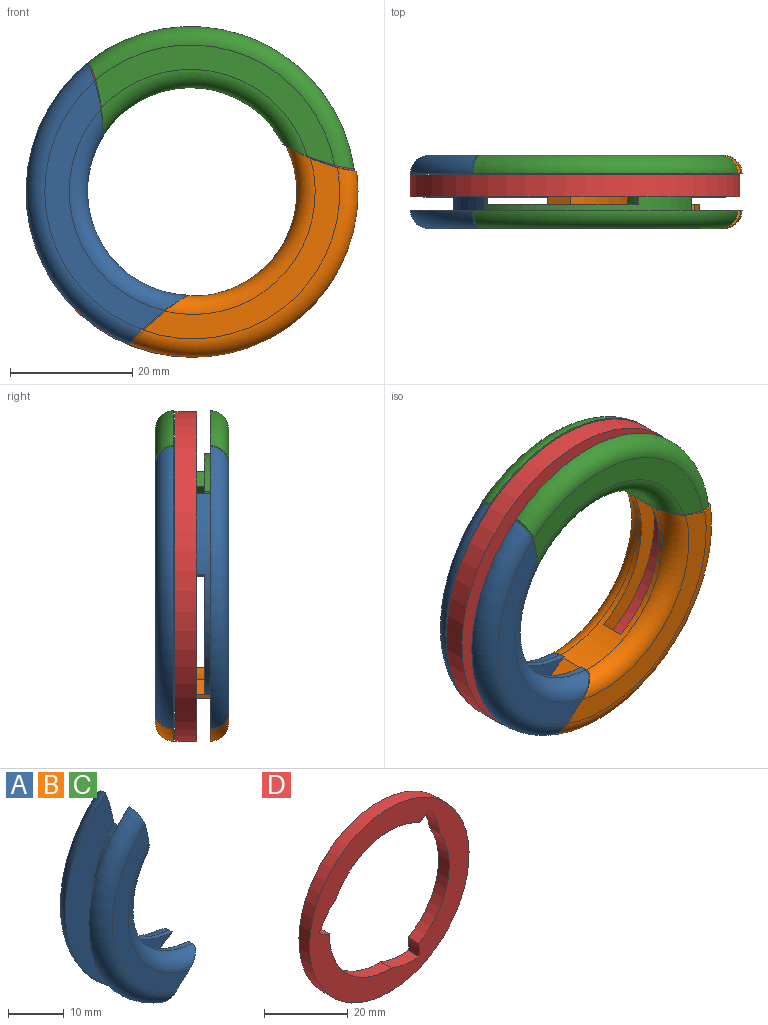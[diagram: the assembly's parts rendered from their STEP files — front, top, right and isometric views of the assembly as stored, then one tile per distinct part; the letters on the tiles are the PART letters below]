
ASSEMBLY  parts=4 mates=6
PART A: 16 faces, bbox 28.5x12x50.5 mm
  f0: cylinder r=20mm len=33.09mm, axis (0,1,0), area 142.1mm2, adj f1,f3,f4,f5,f7,f8,f9,f11
  f1: cylinder r=10mm len=4mm, axis (0,1,0), area 12.1mm2, adj f0,f2,f7,f11
  f2: cylinder r=17mm len=26.09mm, axis (0,1,0), area 109.6mm2, adj f1,f3,f5,f7,f9,f11,f12,f15
  f3: cylinder r=32mm len=12.09mm, axis (0,1,0), area 90.9mm2, adj f0,f2,f4,f6,f8,f10,f12,f13
  f4: plane 46.28x22.57mm, normal (0,-1,0), area 344.5mm2, adj f0,f3,f5,f14
  f5: cylinder r=32mm len=9.29mm, axis (0,-1,0), area 36.5mm2, adj f0,f2,f4,f6,f7,f14,f15
  f6: plane 40.84x19.57mm, normal (0,1,0), area 184.3mm2, adj f3,f5,f14,f15
  f7: plane 19.87x19.3mm, normal (0,-1,0), area 79.3mm2, adj f0,f1,f2,f5
  f8: plane 46.28x22.57mm, normal (0,1,0), area 344.5mm2, adj f0,f3,f9,f13
  f9: cylinder r=32mm len=9.29mm, axis (0,1,0), area 36.5mm2, adj f0,f2,f8,f10,f11,f12,f13
  f10: plane 40.84x19.57mm, normal (0,-1,0), area 184.3mm2, adj f3,f9,f12,f13
  f11: plane 19.87x19.3mm, normal (0,1,0), area 79.3mm2, adj f0,f1,f2,f9
  f12: torus R=20mm, axis (0,1,0), area 178.5mm2, adj f2,f3,f9,f10
  f13: torus R=24mm, axis (0,1,0), area 255.7mm2, adj f3,f8,f9,f10
  f14: torus R=24mm, axis (0,-1,0), area 255.7mm2, adj f3,f4,f5,f6
  f15: torus R=20mm, axis (0,-1,0), area 178.5mm2, adj f2,f3,f5,f6
PART B: same geometry as A
PART C: same geometry as A
PART D: 12 faces, bbox 54x3.6x54 mm
  f0: cylinder r=10.2mm len=3.6mm, axis (0,1,0), area 14mm2, adj f1,f9,f10,f11
  f1: cylinder r=20mm len=7.49mm, axis (0,1,0), area 34.4mm2, adj f0,f2,f10,f11
  f2: cylinder r=20.3mm len=28.28mm, axis (0,1,0), area 118.2mm2, adj f1,f3,f10,f11
  f3: cylinder r=10.2mm len=3.6mm, axis (0,1,0), area 14mm2, adj f2,f4,f10,f11
  f4: cylinder r=20mm len=8.77mm, axis (0,1,0), area 34.4mm2, adj f3,f5,f10,f11
  f5: cylinder r=20.3mm len=28.45mm, axis (0,1,0), area 118.2mm2, adj f4,f6,f10,f11
  f6: cylinder r=10.2mm len=3.87mm, axis (0,1,0), area 14mm2, adj f5,f7,f10,f11
  f7: cylinder r=20mm len=9.38mm, axis (0,1,0), area 34.4mm2, adj f6,f9,f10,f11
  f8: cylinder r=27mm len=54mm, axis (0,1,0), area 610.7mm2, adj f10,f11
  f9: cylinder r=20.3mm len=20.99mm, axis (0,1,0), area 118.2mm2, adj f0,f7,f10,f11
  f10: plane 54x54mm, normal (0,-1,0), area 940.2mm2, adj f0,f1,f2,f3,f4,f5,f6,f7
  f11: plane 54x54mm, normal (0,1,0), area 940.2mm2, adj f0,f1,f2,f3,f4,f5,f6,f7
PLACE A rot(axis=(0,-1,0),0.5deg) t=(-49.09,0.19,8.07)mm
PLACE B rot(axis=(0,-1,0),118.9deg) t=(-48.82,0.19,7.92)mm
PLACE C rot(axis=(0,1,0),120.4deg) t=(-49.23,0.19,8.03)mm
PLACE D t=(-49.17,0.19,7.92)mm fixed
MATE planar C.f4 <-> D.f8  axis (0,-1,0) through (-42.86,0.19,26.52)mm
MATE revolute A.f1 <-> D.f0  axis (0,1,0) through (-66.5,-2.81,17.91)mm
MATE revolute C.f1 <-> D.f3  axis (0,1,0) through (-31.84,-2.81,17.91)mm
MATE planar D.f7 <-> B.f8  axis (0,-1,0) through (-41.15,-3.61,6.24)mm
MATE revolute B.f1 <-> D.f6  axis (0,1,0) through (-49.2,-2.81,-12.08)mm
MATE planar D.f8 <-> A.f4  axis (0,1,0) through (-49.17,-0.01,7.92)mm
